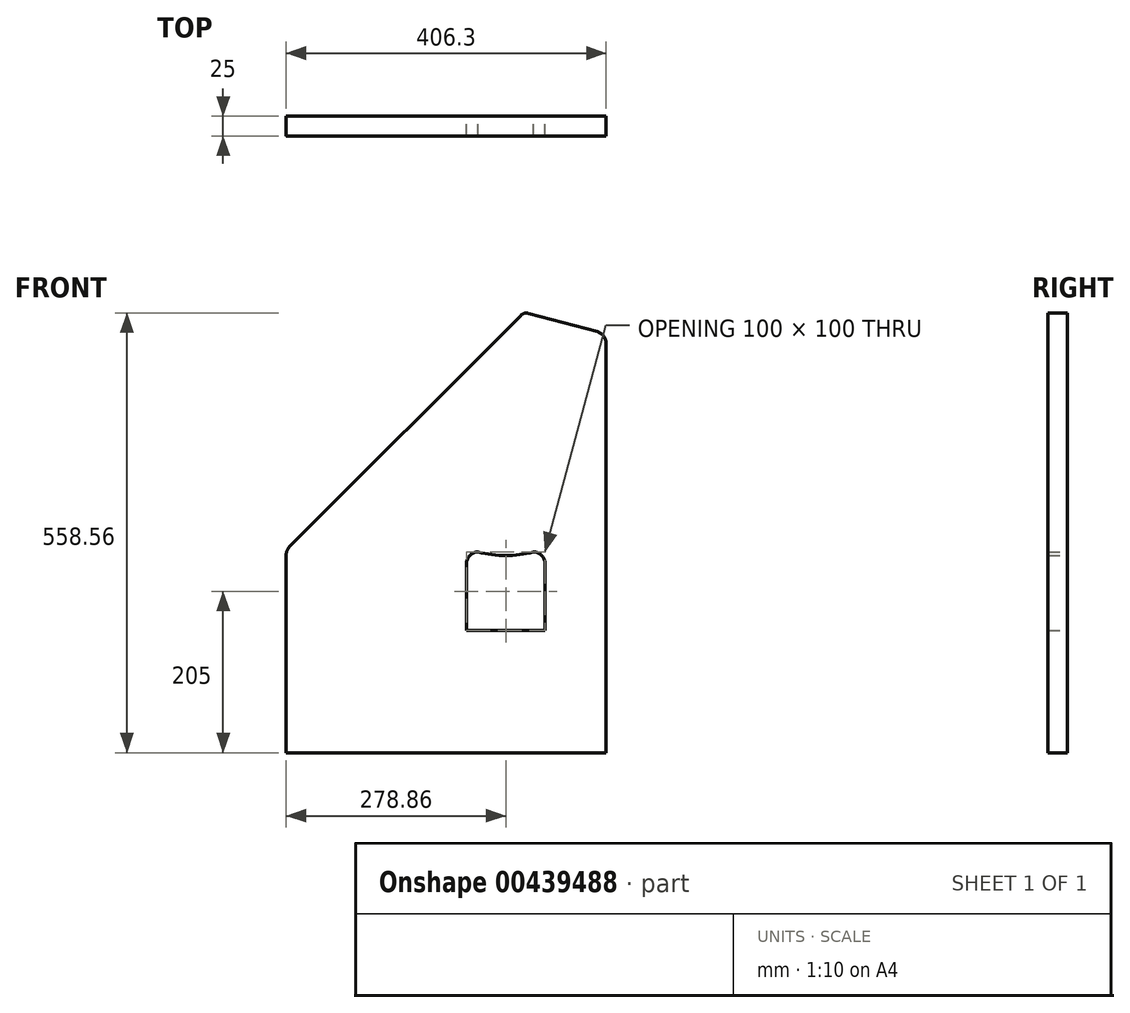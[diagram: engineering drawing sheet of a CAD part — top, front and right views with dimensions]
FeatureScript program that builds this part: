
annotation { "Feature Type Name" : "Feature", "Feature Type Description" : "" }
export const myFeature = defineFeature(function(context is Context, id is Id, definition is map)
    precondition{}
    {
        {
            var Q0;
            Q0=qCreatedBy(makeId("Front.planeOp"),FACE);
            var sketch = newSketch(context, id + "F0", { "sketchPlane" : qUnion([Q0])});
            skLineSegment(sketch, "E0", {"start": v(127.44, -155) * mm, "end": v(-278.86, -155) * mm});
            skLineSegment(sketch, "E1", {"start": v(-278.86, -155) * mm, "end": v(-278.86, 96.39) * mm});
            skLineSegment(sketch, "E2", {"start": v(-274.47, 107) * mm, "end": v(19.17, 400.63) * mm});
            skLineSegment(sketch, "E3", {"start": v(28.83, 403.21) * mm, "end": v(116.32, 379.77) * mm});
            skLineSegment(sketch, "E4", {"start": v(127.44, 365.28) * mm, "end": v(127.44, -155) * mm});
            skLineSegment(sketch, "E5", {"start": v(-273.86, -145) * mm, "end": v(-273.86, 91.28) * mm, "construction": true});
            skLineSegment(sketch, "E6", {"start": v(-278.86, 93.36) * mm, "end": v(25.2, 397.42) * mm, "construction": true});
            skLineSegment(sketch, "E7", {"start": v(25.2, 397.42) * mm, "end": v(120.9, 371.78) * mm, "construction": true});
            skLineSegment(sketch, "E8", {"start": v(112, 361.74) * mm, "end": v(112, -25) * mm, "construction": true});
            skLineSegment(sketch, "E9", {"start": v(100, -137) * mm, "end": v(-261.86, -137) * mm, "construction": true});
            skLineSegment(sketch, "E10", {"start": v(100, -137) * mm, "end": v(100, -155) * mm, "construction": true});
            skLineSegment(sketch, "E11", {"start": v(-261.86, -137) * mm, "end": v(-261.86, -145) * mm, "construction": true});
            skLineSegment(sketch, "E12", {"start": v(-261.86, -145) * mm, "end": v(-273.86, -145) * mm, "construction": true});
            skLineSegment(sketch, "E13", {"start": v(120.9, 371.78) * mm, "end": v(117.8, 360.19) * mm, "construction": true});
            skLineSegment(sketch, "E14", {"start": v(117.8, 360.19) * mm, "end": v(112, 361.74) * mm, "construction": true});
            skLineSegment(sketch, "E15", {"start": v(-273.86, 91.28) * mm, "end": v(20.98, 386.13) * mm, "construction": true});
            skLineSegment(sketch, "E16", {"start": v(112, 361.74) * mm, "end": v(15.4, 387.62) * mm, "construction": true});
            skPoint(sketch, "E17.visualSharp", {"position": v(-278.86, 102.6) * mm});
            skArc(sketch, "E17.filletArc", {"start": v(-274.47, 107) * mm, "mid": v(-277.72, 102.13) * mm, "end": v(-278.86, 96.39) * mm});
            skPoint(sketch, "E18.visualSharp", {"position": v(23.25, 404.7) * mm});
            skArc(sketch, "E18.filletArc", {"start": v(28.83, 403.21) * mm, "mid": v(23.65, 403.21) * mm, "end": v(19.17, 400.63) * mm});
            skPoint(sketch, "E19.visualSharp", {"position": v(127.44, 376.8) * mm});
            skArc(sketch, "E19.filletArc", {"start": v(127.44, 365.28) * mm, "mid": v(124.34, 374.41) * mm, "end": v(116.32, 379.77) * mm});
            skLineSegment(sketch, "E20", {"start": v(23.65, 403.21) * mm, "end": v(26.24, 393.56) * mm, "construction": true});
            skLineSegment(sketch, "E21.left", {"start": v(50, 30) * mm, "end": v(50, 85) * mm});
            skLineSegment(sketch, "E21.right", {"start": v(-50, 30) * mm, "end": v(-50, 85) * mm});
            skPoint(sketch, "E21.middle", {"position": v(0, 0) * mm});
            skArc(sketch, "E22.filletArc", {"start": v(-35, 100) * mm, "mid": v(-45.6, 95.6) * mm, "end": v(-50, 85) * mm});
            skArc(sketch, "E23.filletArc", {"start": v(50, 85) * mm, "mid": v(45.6, 95.6) * mm, "end": v(35, 100) * mm});
            skLineSegment(sketch, "E24", {"start": v(-261.86, 103.28) * mm, "end": v(-233.57, 75) * mm, "construction": true});
            skLineSegment(sketch, "E25", {"start": v(-233.57, 75) * mm, "end": v(65.6, 374.17) * mm, "construction": true});
            skLineSegment(sketch, "E26", {"start": v(112.44, 365.28) * mm, "end": v(124.34, 374.41) * mm, "construction": true});
            skLineSegment(sketch, "E27", {"start": v(100, -125) * mm, "end": v(100, -37) * mm, "construction": true});
            skLineSegment(sketch, "E28", {"start": v(100, -25) * mm, "end": v(88, -25) * mm, "construction": true});
            skLineSegment(sketch, "E29", {"start": v(88, -25) * mm, "end": v(88, -113) * mm, "construction": true});
            skLineSegment(sketch, "E30", {"start": v(88, -125) * mm, "end": v(100, -125) * mm, "construction": true});
            skLineSegment(sketch, "E31", {"start": v(100, -25) * mm, "end": v(100, 364.95) * mm, "construction": true});
            skLineSegment(sketch, "E32", {"start": v(-82, -125) * mm, "end": v(-261.86, -125) * mm, "construction": true});
            skLineSegment(sketch, "E33", {"start": v(-82, -125) * mm, "end": v(88, -125) * mm, "construction": true});
            skLineSegment(sketch, "E34", {"start": v(-82, -125) * mm, "end": v(-82, 55) * mm, "construction": true});
            skLineSegment(sketch, "E35", {"start": v(88, 55) * mm, "end": v(-82, 55) * mm, "construction": true});
            skLineSegment(sketch, "E36", {"start": v(88, -25) * mm, "end": v(88, 55) * mm, "construction": true});
            skLineSegment(sketch, "E37", {"start": v(-50, 30) * mm, "end": v(-55, 30) * mm, "construction": true});
            skLineSegment(sketch, "E38", {"start": v(55, 30) * mm, "end": v(50, 30) * mm, "construction": true});
            skLineSegment(sketch, "E39", {"start": v(-55, 30) * mm, "end": v(-55, 200) * mm, "construction": true});
            skLineSegment(sketch, "E40", {"start": v(55, 200) * mm, "end": v(55, 30) * mm, "construction": true});
            skLineSegment(sketch, "E41", {"start": v(127.44, -25) * mm, "end": v(112, -25) * mm, "construction": true});
            skLineSegment(sketch, "E42", {"start": v(-261.86, -25) * mm, "end": v(-261.86, -37) * mm, "construction": true});
            skLineSegment(sketch, "E43", {"start": v(-261.86, -37) * mm, "end": v(88, -37) * mm, "construction": true});
            skLineSegment(sketch, "E44", {"start": v(127.44, -37) * mm, "end": v(127.44, -25) * mm, "construction": true});
            skLineSegment(sketch, "E45", {"start": v(100, -37) * mm, "end": v(100, -25) * mm, "construction": true});
            skLineSegment(sketch, "E46", {"start": v(88, -37) * mm, "end": v(100, -37) * mm, "construction": true});
            skLineSegment(sketch, "E47", {"start": v(112, -37) * mm, "end": v(112, -155) * mm, "construction": true});
            skLineSegment(sketch, "E48", {"start": v(112, -25) * mm, "end": v(112, -37) * mm, "construction": true});
            skLineSegment(sketch, "E49", {"start": v(-261.86, -25) * mm, "end": v(-261.86, -25) * mm});
            skLineSegment(sketch, "E50", {"start": v(-261.86, -25) * mm, "end": v(-261.86, 103.28) * mm, "construction": true});
            skLineSegment(sketch, "E51", {"start": v(-273.86, 91.28) * mm, "end": v(-278.86, 86.28) * mm, "construction": true});
            skLineSegment(sketch, "E52", {"start": v(-233.57, 75) * mm, "end": v(-225.09, 66.51) * mm, "construction": true});
            skLineSegment(sketch, "E53", {"start": v(-225.09, 66.51) * mm, "end": v(78.98, 370.59) * mm, "construction": true});
            skArc(sketch, "E54", {"start": v(-35, 100) * mm, "mid": v(0, 95.55) * mm, "end": v(35, 100) * mm});
            skLineSegment(sketch, "E55", {"start": v(-55, 200) * mm, "end": v(-67, 200) * mm, "construction": true});
            skLineSegment(sketch, "E56", {"start": v(-67, 200) * mm, "end": v(-67, 0) * mm, "construction": true});
            skLineSegment(sketch, "E57", {"start": v(55, 200) * mm, "end": v(67, 200) * mm, "construction": true});
            skLineSegment(sketch, "E58", {"start": v(-50, 30) * mm, "end": v(-50, 0) * mm});
            skLineSegment(sketch, "E59", {"start": v(-50, 0) * mm, "end": v(-67, 0) * mm, "construction": true});
            skLineSegment(sketch, "E60", {"start": v(50, 30) * mm, "end": v(50, 0) * mm});
            skLineSegment(sketch, "E61", {"start": v(-50, 0) * mm, "end": v(50, 0) * mm});
            skLineSegment(sketch, "E62", {"start": v(67, 200) * mm, "end": v(67, 0) * mm, "construction": true});
            skLineSegment(sketch, "E63", {"start": v(67, 0) * mm, "end": v(50, 0) * mm, "construction": true});
            skLineSegment(sketch, "E64", {"start": v(-55, 200) * mm, "end": v(55, 200) * mm, "construction": true});
            skLineSegment(sketch, "E65", {"start": v(-55, 188) * mm, "end": v(55, 188) * mm, "construction": true});
            skLineSegment(sketch, "E66", {"start": v(40.48, -137) * mm, "end": v(100, -137) * mm, "construction": true});
            skLineSegment(sketch, "E67", {"start": v(100, -125) * mm, "end": v(40.48, -125) * mm, "construction": true});
            skLineSegment(sketch, "E68", {"start": v(-261.86, -125) * mm, "end": v(-261.86, -37) * mm, "construction": true});
            skLineSegment(sketch, "E69", {"start": v(-261.86, -125) * mm, "end": v(-265.86, -125) * mm, "construction": true});
            skLineSegment(sketch, "E70", {"start": v(-265.86, -125) * mm, "end": v(-265.86, -137) * mm, "construction": true});
            skLineSegment(sketch, "E71", {"start": v(-265.86, -137) * mm, "end": v(-261.86, -137) * mm, "construction": true});
            skLineSegment(sketch, "E72", {"start": v(100, -125) * mm, "end": v(100, -137) * mm, "construction": true});
            skLineSegment(sketch, "E73", {"start": v(67, 0) * mm, "end": v(67, -4) * mm, "construction": true});
            skLineSegment(sketch, "E74", {"start": v(67, -4) * mm, "end": v(-67, -4) * mm, "construction": true});
            skLineSegment(sketch, "E75", {"start": v(-67, -4) * mm, "end": v(-67, 0) * mm, "construction": true});
            skLineSegment(sketch, "E76", {"start": v(88, -25) * mm, "end": v(-261.86, -25) * mm, "construction": true});
            skLineSegment(sketch, "E77", {"start": v(112, -25) * mm, "end": v(100, -25) * mm, "construction": true});
            skLineSegment(sketch, "E78", {"start": v(112, -37) * mm, "end": v(127.44, -37) * mm, "construction": true});
            skLineSegment(sketch, "E79", {"start": v(100, -37) * mm, "end": v(112, -37) * mm, "construction": true});
            skLineSegment(sketch, "E80", {"start": v(88, -113) * mm, "end": v(100, -113) * mm, "construction": true});
            skLineSegment(sketch, "E81", {"start": v(88, -113) * mm, "end": v(88, -125) * mm, "construction": true});
            skLineSegment(sketch, "E82", {"start": v(88, 55) * mm, "end": v(88, 51) * mm, "construction": true});
            skLineSegment(sketch, "E83", {"start": v(88, 51) * mm, "end": v(112, 51) * mm, "construction": true});
            skLineSegment(sketch, "E84", {"start": v(79, 14) * mm, "end": v(79, 100) * mm, "construction": true});
            skLineSegment(sketch, "E85", {"start": v(79, 100) * mm, "end": v(67, 100) * mm, "construction": true});
            skLineSegment(sketch, "E86", {"start": v(88, 55) * mm, "end": v(67, 55) * mm, "construction": true});
            skLineSegment(sketch, "E87", {"start": v(67, 55) * mm, "end": v(67, 63) * mm, "construction": true});
            skLineSegment(sketch, "E88", {"start": v(67, 63) * mm, "end": v(112, 63) * mm, "construction": true});
            skLineSegment(sketch, "E89", {"start": v(112, 63) * mm, "end": v(112, 51) * mm, "construction": true});
            skLineSegment(sketch, "E90", {"start": v(112, 63) * mm, "end": v(127.44, 63) * mm, "construction": true});
            skLineSegment(sketch, "E91", {"start": v(127.44, 63) * mm, "end": v(127.44, 51) * mm, "construction": true});
            skLineSegment(sketch, "E92", {"start": v(127.44, 51) * mm, "end": v(112, 51) * mm, "construction": true});
            skLineSegment(sketch, "E93", {"start": v(88, 51) * mm, "end": v(67, 51) * mm, "construction": true});
            skLineSegment(sketch, "E94", {"start": v(67, 14) * mm, "end": v(79, 14) * mm, "construction": true});
            skLineSegment(sketch, "E95", {"start": v(79, 51) * mm, "end": v(79, 14) * mm, "construction": true});
            skLineSegment(sketch, "E96", {"start": v(79, 63) * mm, "end": v(79, 100) * mm, "construction": true});
            skSolve(sketch);
        }
        {
            var Q0;
            Q0=makeQuery(id+"F0.imprint","IMPRINT",FACE,{"disambiguationData":[TD([[makeQuery(id+"F0.imprint","IMPRINT",EDGE,{"derivedFrom":sQuery(id+"F0.wireOp",EDGE,"E0")}),-1.0]])]});
            extrude(context, id + "F1", {"entities" : qUnion([Q0]), "depth" : 25 * mm, "offsetDistance" : 25 * mm});
        }
    });
